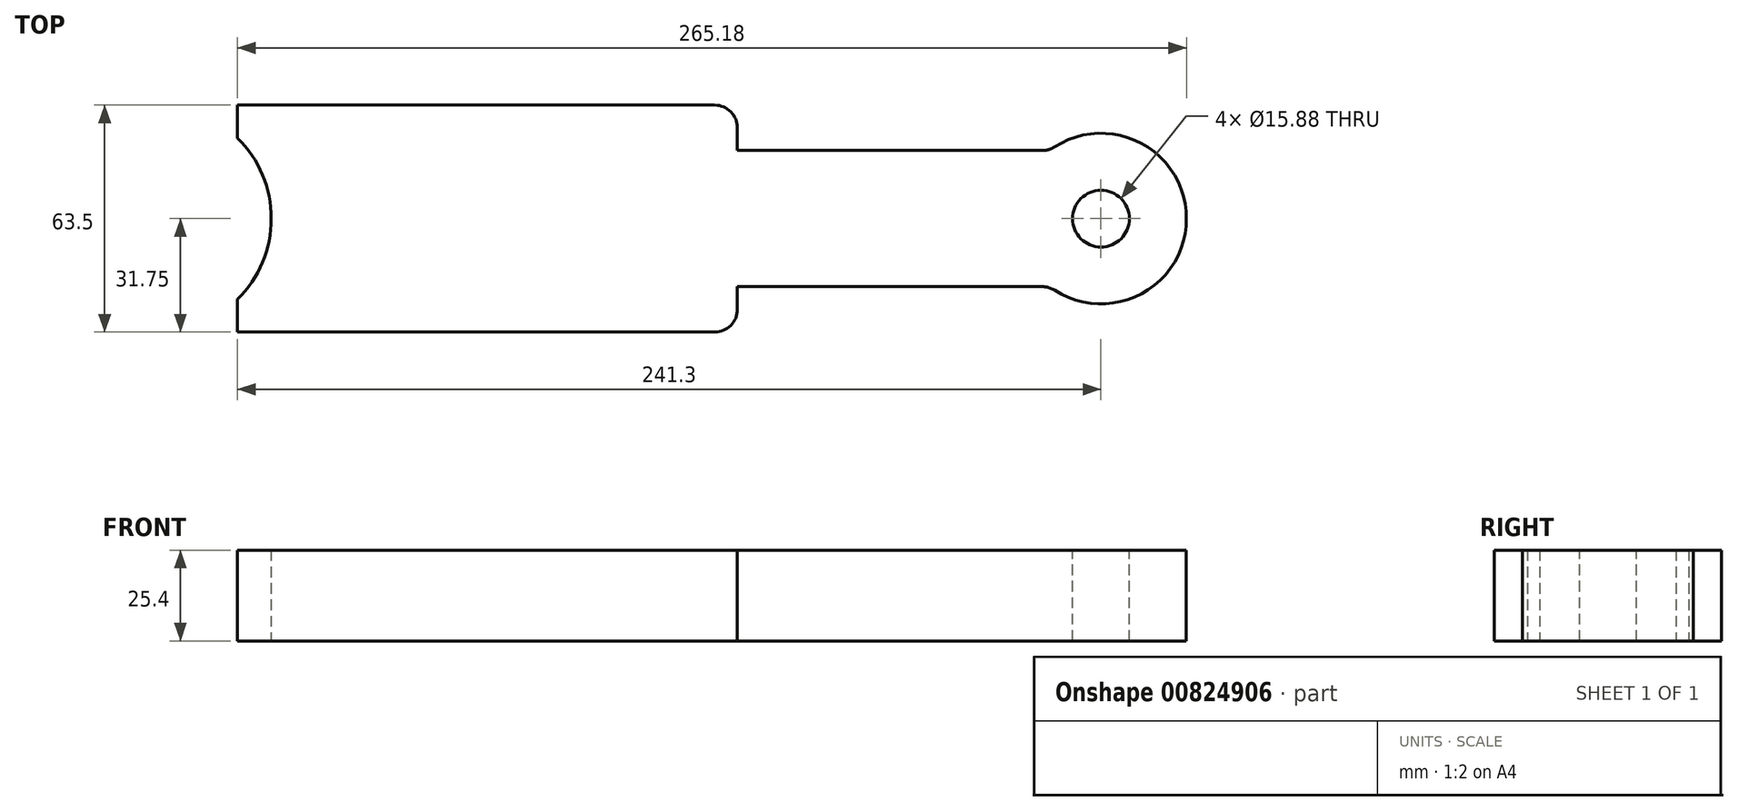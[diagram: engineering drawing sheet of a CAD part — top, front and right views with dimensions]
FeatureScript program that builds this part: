
annotation { "Feature Type Name" : "Feature", "Feature Type Description" : "" }
export const myFeature = defineFeature(function(context is Context, id is Id, definition is map)
    precondition{}
    {
        {
            var Q0;
            Q0=qCreatedBy(makeId("Top.planeOp"),FACE);
            var sketch = newSketch(context, id + "F0", { "sketchPlane" : qUnion([Q0])});
            skLineSegment(sketch, "E0.bottom", {"start": v(0, 0) * mm, "end": v(139.7, 0) * mm});
            skLineSegment(sketch, "E0.top", {"start": v(0, 63.5) * mm, "end": v(139.7, 63.5) * mm});
            skLineSegment(sketch, "E0.left", {"start": v(0, 0) * mm, "end": v(0, 9.2) * mm});
            skLineSegment(sketch, "E0.right", {"start": v(139.7, 0) * mm, "end": v(139.7, 12.7) * mm});
            skLineSegment(sketch, "E1.bottom", {"start": v(139.7, 50.8) * mm, "end": v(226.9, 50.8) * mm});
            skLineSegment(sketch, "E1.top", {"start": v(139.7, 12.7) * mm, "end": v(226.9, 12.7) * mm});
            skArc(sketch, "E2", {"start": v(226.9, 12.7) * mm, "mid": v(265.18, 31.75) * mm, "end": v(226.9, 50.8) * mm});
            skLineSegment(sketch, "E3", {"start": v(0, 31.75) * mm, "end": v(357.89, 31.75) * mm, "construction": true});
            skLineSegment(sketch, "E4.trimOffspring", {"start": v(139.7, 50.8) * mm, "end": v(139.7, 63.5) * mm});
            skArc(sketch, "E5", {"start": v(0, 9.2) * mm, "mid": v(9.4, 31.75) * mm, "end": v(0, 54.3) * mm});
            skLineSegment(sketch, "E6.trimOffspring", {"start": v(0, 54.3) * mm, "end": v(0, 63.5) * mm});
            skSolve(sketch);
        }
        {
            var Q0;
            Q0 = qSketchRegion(id + "F0", true);
            extrude(context, id + "F1", {"entities" : qUnion([Q0]), "depth" : 25.4 * mm, "offsetDistance" : 25.4 * mm});
        }
        {
            var Q0;
            Q0=makeQuery(id+"F1.opExtrude","SWEPT_EDGE",EDGE,{"disambiguationData":[OSD([sQuery(id+"F0.wireOp",EDGE,"E0.bottom"),sQuery(id+"F0.wireOp",EDGE,"E0.right")])]});
            var Q1;
            Q1=makeQuery(id+"F1.opExtrude","SWEPT_EDGE",EDGE,{"disambiguationData":[OSD([sQuery(id+"F0.wireOp",EDGE,"E0.top"),sQuery(id+"F0.wireOp",EDGE,"E4.trimOffspring")])]});
            var Q2;
            Q2=makeQuery(id+"F1.opExtrude","SWEPT_EDGE",EDGE,{"disambiguationData":[OSD([sQuery(id+"F0.wireOp",EDGE,"E1.top"),sQuery(id+"F0.wireOp",EDGE,"E2")])]});
            var Q3;
            Q3=makeQuery(id+"F1.opExtrude","SWEPT_EDGE",EDGE,{"disambiguationData":[OSD([sQuery(id+"F0.wireOp",EDGE,"E1.bottom"),sQuery(id+"F0.wireOp",EDGE,"E2")])]});
            fillet(context, id + "F2", {"entities" : qUnion([Q0, Q1, Q2, Q3]), "radius" : 6.35 * mm, "tangentPropagation" : true, "allowEdgeOverflow" : false});
        }
        {
            var Q0;
            Q0=makeQuery(id+"F1.opExtrude","CAP_FACE",FACE,{"disambiguationData":[OSD([sQuery(id+"F0.wireOp",EDGE,"E0.bottom"),sQuery(id+"F0.wireOp",EDGE,"E0.top"),sQuery(id+"F0.wireOp",EDGE,"E0.left"),sQuery(id+"F0.wireOp",EDGE,"E0.right"),sQuery(id+"F0.wireOp",EDGE,"E1.bottom"),sQuery(id+"F0.wireOp",EDGE,"E1.top"),sQuery(id+"F0.wireOp",EDGE,"E2"),sQuery(id+"F0.wireOp",EDGE,"E4.trimOffspring"),sQuery(id+"F0.wireOp",EDGE,"E5"),sQuery(id+"F0.wireOp",EDGE,"E6.trimOffspring")])],"isStart":false});
            var sketch = newSketch(context, id + "F3", { "sketchPlane" : qUnion([Q0])});
            skCircle(sketch, "E7", {"center": v(241.3, 31.75) * mm, "radius": 7.94 * mm});
            skSolve(sketch);
        }
        {
            var Q0;
            Q0 = qSketchRegion(id + "F3", true);
            extrude(context, id + "F4", {"entities" : qUnion([Q0]), "operationType" : NewBodyOperationType.REMOVE, "endBound" : BoundingType.THROUGH_ALL, "oppositeDirection" : true, "depth" : 25.4 * mm, "offsetDistance" : 25.4 * mm});
        }
    });
